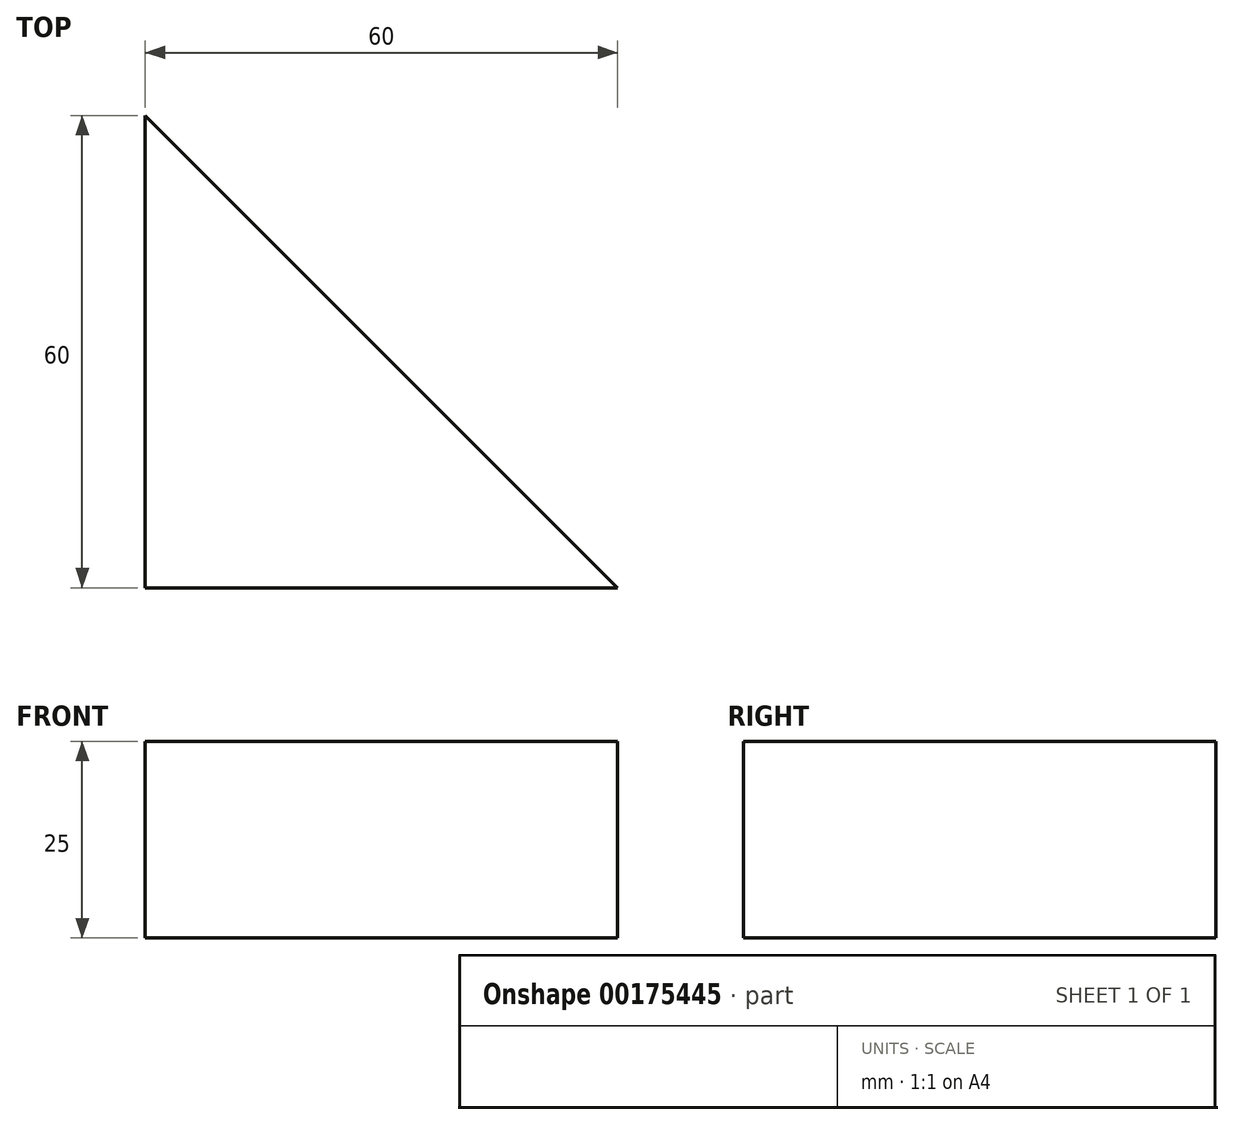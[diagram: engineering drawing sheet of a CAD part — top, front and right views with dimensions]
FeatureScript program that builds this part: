
annotation { "Feature Type Name" : "Feature", "Feature Type Description" : "" }
export const myFeature = defineFeature(function(context is Context, id is Id, definition is map)
    precondition{}
    {
        {
            var Q0;
            Q0=qCreatedBy(makeId("Top.planeOp"),FACE);
            var sketch = newSketch(context, id + "F0", { "sketchPlane" : qUnion([Q0])});
            skLineSegment(sketch, "E0", {"start": v(-30.49, 49.4) * mm, "end": v(-30.49, -10.6) * mm});
            skLineSegment(sketch, "E1", {"start": v(-30.49, -10.6) * mm, "end": v(29.51, -10.6) * mm});
            skLineSegment(sketch, "E2", {"start": v(29.51, -10.6) * mm, "end": v(-30.49, 49.4) * mm});
            skSolve(sketch);
        }
        {
            var Q0;
            Q0=qCreatedBy(makeId("Top.planeOp"),FACE);
            var sketch = newSketch(context, id + "F1", { "sketchPlane" : qUnion([Q0])});
            skSolve(sketch);
        }
        {
            var Q0;
            Q0 = qSketchRegion(id + "F1", true);
            var Q1;
            Q1=makeQuery(id+"F0.imprint","IMPRINT",FACE,{"disambiguationData":[TD([[makeQuery(id+"F0.imprint","IMPRINT",EDGE,{"derivedFrom":sQuery(id+"F0.wireOp",EDGE,"E0")}),1.0]])]});
            extrude(context, id + "F2", {"entities" : qUnion([Q0, Q1]), "depth" : 25 * mm});
        }
    });
